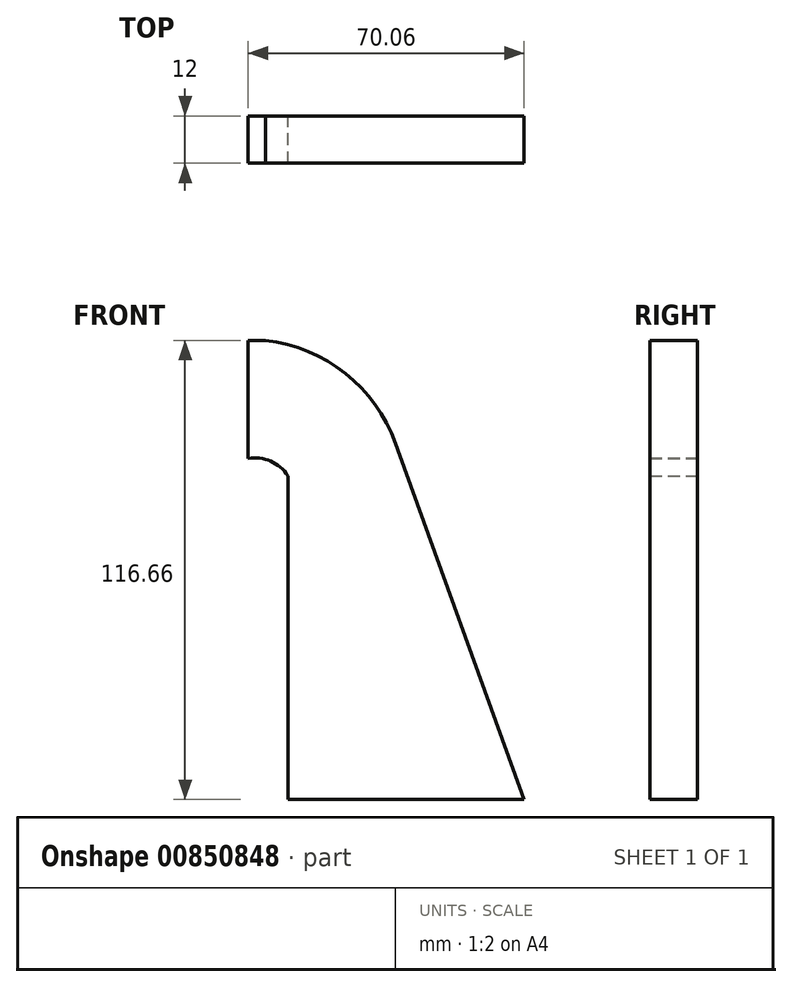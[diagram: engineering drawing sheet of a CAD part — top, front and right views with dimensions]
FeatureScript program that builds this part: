
annotation { "Feature Type Name" : "Feature", "Feature Type Description" : "" }
export const myFeature = defineFeature(function(context is Context, id is Id, definition is map)
    precondition{}
    {
        {
            var Q0;
            Q0=qCreatedBy(makeId("Front.planeOp"),FACE);
            var sketch = newSketch(context, id + "F0", { "sketchPlane" : qUnion([Q0])});
            skLineSegment(sketch, "E0", {"start": v(-126.07, -74.32) * mm, "end": v(-186.07, -74.32) * mm});
            skLineSegment(sketch, "E1", {"start": v(-196.13, 12.34) * mm, "end": v(-196.13, 42.34) * mm});
            skLineSegment(sketch, "E2", {"start": v(-186.07, -74.32) * mm, "end": v(-186.07, 7.94) * mm});
            skArc(sketch, "E3", {"start": v(-186.07, 7.94) * mm, "mid": v(-190.44, 11.64) * mm, "end": v(-196.13, 12.34) * mm});
            skLineSegment(sketch, "E4", {"start": v(-196.13, 42.34) * mm, "end": v(-191.7, 42.34) * mm});
            skLineSegment(sketch, "E5", {"start": v(-158.68, 16.16) * mm, "end": v(-126.07, -74.32) * mm});
            skArc(sketch, "E6", {"start": v(-158.68, 16.16) * mm, "mid": v(-171.46, 33.95) * mm, "end": v(-191.7, 42.34) * mm});
            skSolve(sketch);
        }
        {
            var Q0;
            Q0=makeQuery(id+"F0.imprint","IMPRINT",FACE,{"disambiguationData":[TD([[makeQuery(id+"F0.imprint","IMPRINT",EDGE,{"derivedFrom":sQuery(id+"F0.wireOp",EDGE,"E0")}),-1.0]])]});
            extrude(context, id + "F1", {"entities" : qUnion([Q0]), "depth" : 12 * mm, "offsetDistance" : 25.4 * mm});
        }
    });
